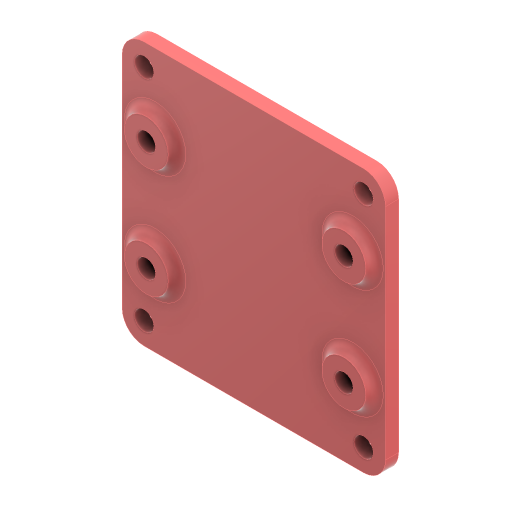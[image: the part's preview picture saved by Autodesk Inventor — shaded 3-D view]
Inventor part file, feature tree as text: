
AUTODESK INVENTOR PART (.ipt)
format: ipt  version: 2023 (Build 270158000, 158)  size: 206,336 bytes
history: native  units: mm
features: extrude x3, sketch x2, fillet x2
ambient origin geometry x8: Origin, YZ Plane, XZ Plane, XY Plane, X Axis, Y Axis, Z Axis, Center Point
bodies: Solid1 (feature_tree)
feature tree (7):
  sketch  "Sketch1"  dims[d0=60.0mm d1=60.0mm]
  extrude  "Extrusion1"  Depth=60.0mm
  extrude  "Extrusion2"  Depth=5.0mm
  fillet  "Fillet1"  Radius=5.0mm
  extrude  "Extrusion3"  Depth=5.0mm
  sketch  "Sketch Driven Pattern1"  dims[d2=50.0mm d3=50.0mm d4=5.0mm d5=5.0mm d6=4.4mm d7=4.4mm d8=4.4mm d9=4.4mm d10=45.0mm d11=25.0mm d12=17.5mm d13=7.5mm d14=10.0mm d15=4.2mm d16=3.0mm d17=0.0mm d18=2.0mm d19=0.0mm d20=2.0mm d21=0.0mm d22=0.0mm d23=5.0mm]
  fillet  "Fillet2"  Radius=4.4mm
